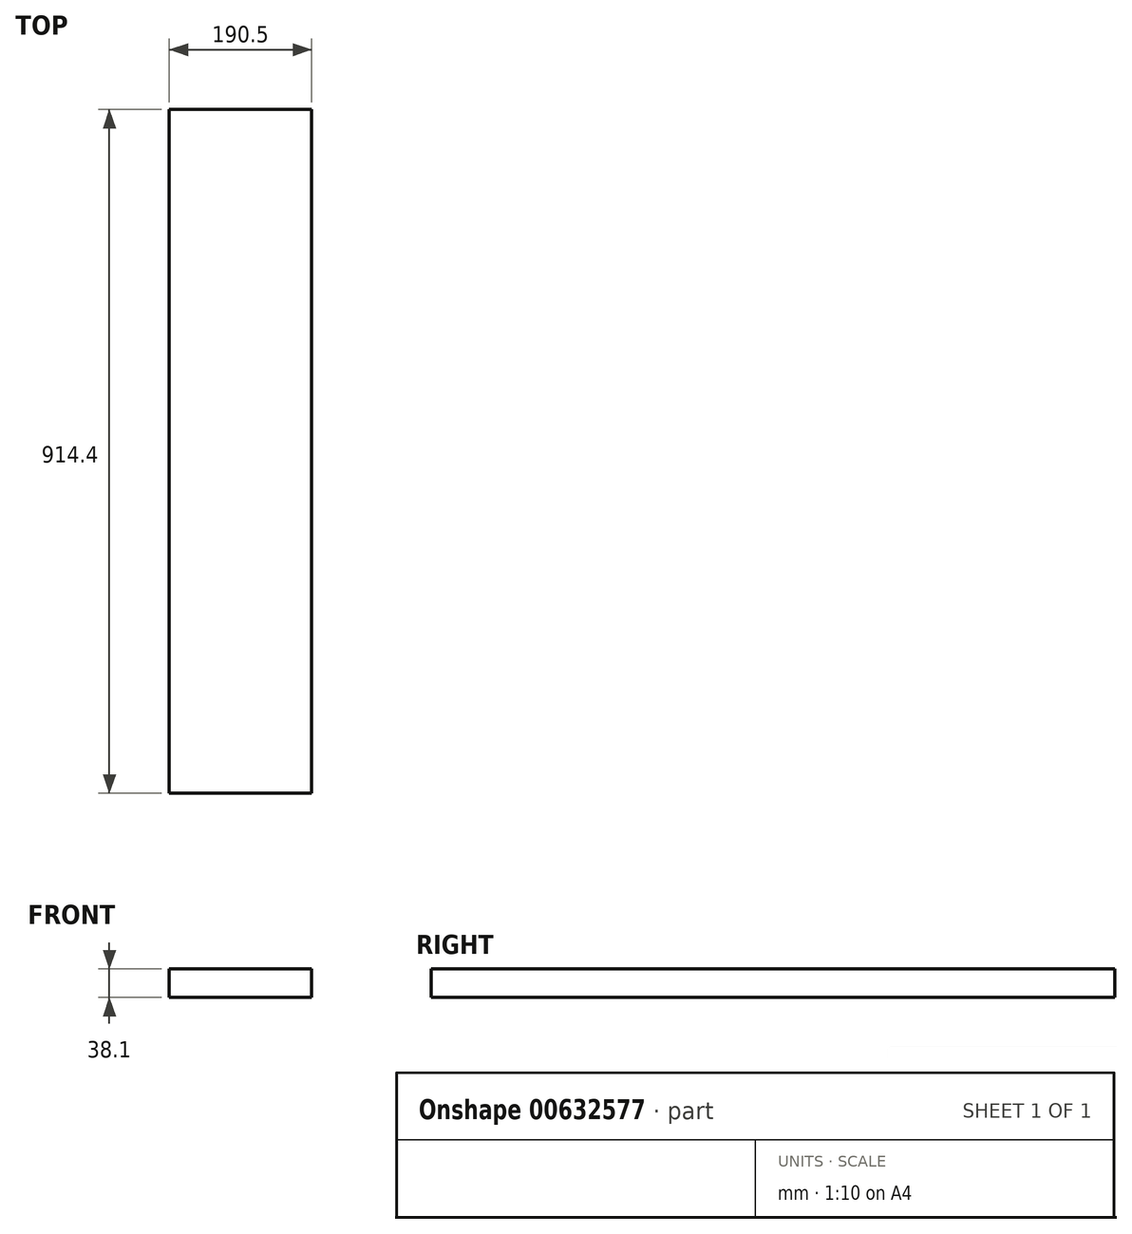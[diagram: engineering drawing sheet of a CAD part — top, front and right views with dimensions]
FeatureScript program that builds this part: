
annotation { "Feature Type Name" : "Feature", "Feature Type Description" : "" }
export const myFeature = defineFeature(function(context is Context, id is Id, definition is map)
    precondition{}
    {
        {
            var Q0;
            Q0=qCreatedBy(makeId("Top.planeOp"),FACE);
            var sketch = newSketch(context, id + "F0", { "sketchPlane" : qUnion([Q0])});
            skLineSegment(sketch, "E0.bottom", {"start": v(-26.9, 882.1) * mm, "end": v(163.6, 882.1) * mm});
            skLineSegment(sketch, "E0.top", {"start": v(-26.9, -32.3) * mm, "end": v(163.6, -32.3) * mm});
            skLineSegment(sketch, "E0.left", {"start": v(-26.9, 882.1) * mm, "end": v(-26.9, -32.3) * mm});
            skLineSegment(sketch, "E0.right", {"start": v(163.6, 882.1) * mm, "end": v(163.6, -32.3) * mm});
            skSolve(sketch);
        }
        {
            var Q0;
            Q0 = qSketchRegion(id + "F0", true);
            extrude(context, id + "F1", {"entities" : qUnion([Q0]), "depth" : 38.1 * mm, "offsetDistance" : 25.4 * mm});
        }
    });
